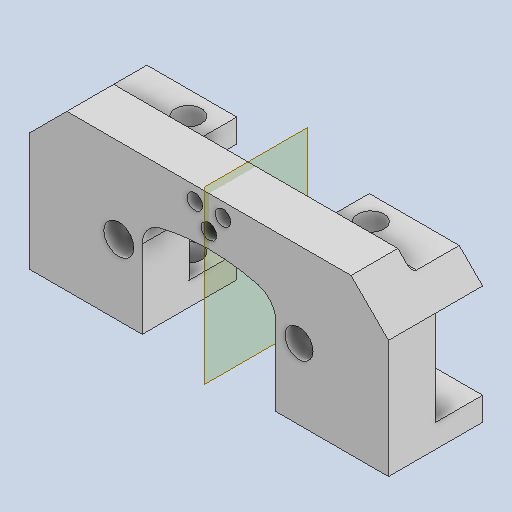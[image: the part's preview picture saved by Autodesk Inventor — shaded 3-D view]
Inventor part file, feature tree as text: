
AUTODESK INVENTOR PART (.ipt)
format: ipt  version: 2022 (Build 260153000, 153)  size: 229,888 bytes
history: native  units: in
note: dims shown in document units (in); Inventor stores cm internally (conversion verified against a paired STEP export)
features: reference x6, extrude x5, sketch x5, plane x4, other x4, fillet x1, mirror x1, projected_geometry x1
ambient origin geometry x8: Origin, YZ Plane, XZ Plane, XY Plane, X Axis, Y Axis, Z Axis, Center Point
bodies: Solid1 (feature_tree)
feature tree (27):
  extrude  "Extrusion1"  Depth=0.0039in
  plane  "Work Plane1"
  extrude  "Extrusion3"  Depth=0.0039in
  sketch  "Sketch4"  dims[d4=0.0039in d5=0.0039in]
  plane  "Work Plane2"
  extrude  "Extrusion4"  Depth=0.0039in
  extrude  "Extrusion5"  Depth=0.315in
  extrude  "Extrusion6"  Depth=0.0394in
  fillet  "Fillet2"  Radius=0.1181in
  plane  "Work Plane3"
  mirror  "Mirror1"
  sketch  "Sketch1"  dims[d0=0.0039in d1=0.0039in]
  reference  "Reference1"
  reference  "Reference2"
  reference  "Reference3"
  sketch  "Sketch3"  dims[d2=0.0039in d3=0.0039in]
  reference  "Reference4"
  projected_geometry  "Projected Loop2"
  sketch  "Sketch5"  dims[d7=1.5748in d9=0.315in]
  reference  "Reference5"
  sketch  "Sketch6"  dims[d10=0.1181in d11=0.1299in d12=0.1181in d13=45.0deg d14=0.3937in d15=0.0in d16=0.1969in d17=0.1299in d19=0.2756in d25=0.1969in d26=0.7874in d27=0.0in d28=0.0039in d29=0.3937in d30=0.0in d31=0.1181in d32=0.0in d33=0.0118in d34=0.0in d35=0.0in d36=0.0394in]
  reference  "Reference6"
  plane  "Work Plane4"
  other  "<userpath>\OneDrive - Imperial College London\ROBOICP\Final Assembly\Final Assembly.iam"
  other  "Final Assembly.iam"
  other  "Guide rod bottom stand (independent):1"
  other  "cantilever:1"
